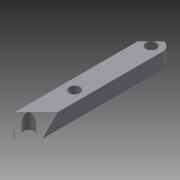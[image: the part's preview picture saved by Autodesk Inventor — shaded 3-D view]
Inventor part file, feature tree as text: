
AUTODESK INVENTOR PART (.ipt)
format: ipt  version: 2015 (Build 190159000, 159)  size: 91,648 bytes
history: native  units: mm
features: extrude x3, sketch x3
ambient origin geometry x8: Origin, YZ Plane, XZ Plane, XY Plane, X Axis, Y Axis, Z Axis, Center Point
bodies: Solid1 (feature_tree)
feature tree (6):
  extrude  "Extrusion1"  Depth=40.0mm
  extrude  "Extrusion2"  Depth=5.0mm TaperAngle=0.0deg
  extrude  "Extrusion3"  Depth=3.5mm
  sketch  "Sketch1"  dims[d0=7.0mm d1=40.0mm]
  sketch  "Sketch2"  dims[d2=7.0mm d3=5.0mm d4=0.0mm]
  sketch  "Sketch3"  dims[d5=3.5mm d6=3.5mm d7=5.0mm d8=0.0mm d9=15.0mm d10=3.5mm d11=10.0mm d12=0.0mm]
